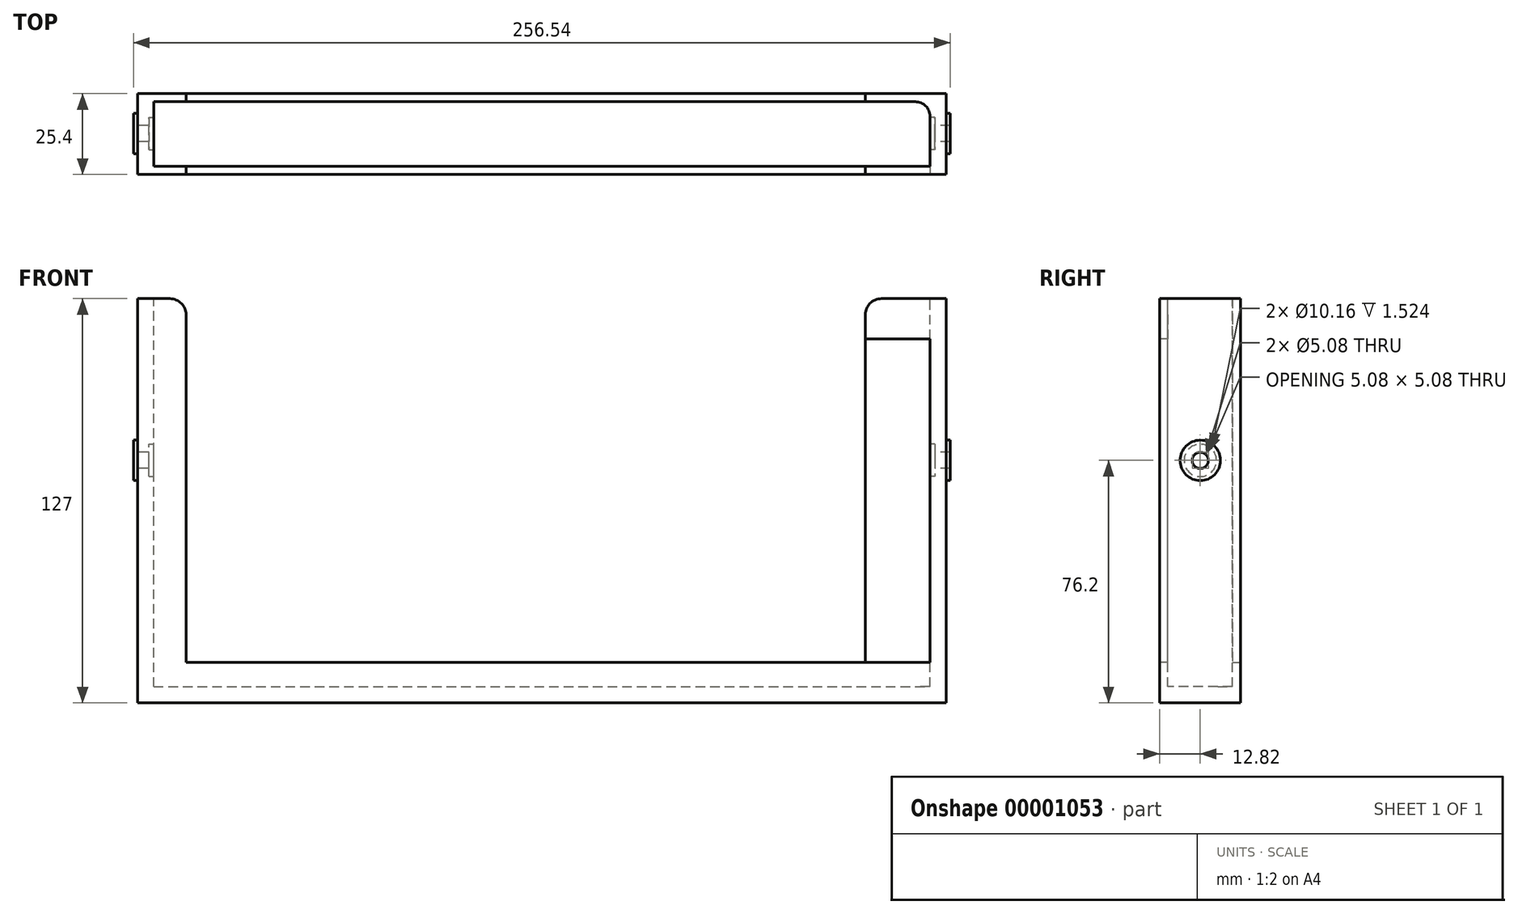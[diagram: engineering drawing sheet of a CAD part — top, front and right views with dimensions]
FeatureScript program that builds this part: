
annotation { "Feature Type Name" : "Feature", "Feature Type Description" : "" }
export const myFeature = defineFeature(function(context is Context, id is Id, definition is map)
    precondition{}
    {
        {
            var Q0;
            Q0=qCreatedBy(makeId("Front.planeOp"),FACE);
            var sketch = newSketch(context, id + "F0", { "sketchPlane" : qUnion([Q0])});
            skLineSegment(sketch, "E0", {"start": v(-127, 127) * mm, "end": v(-127, 0) * mm});
            skLineSegment(sketch, "E1", {"start": v(-127, 0) * mm, "end": v(127, 0) * mm});
            skLineSegment(sketch, "E2", {"start": v(127, 0) * mm, "end": v(127, 127) * mm});
            skLineSegment(sketch, "E3", {"start": v(127, 127) * mm, "end": v(101.6, 127) * mm});
            skLineSegment(sketch, "E4", {"start": v(101.6, 127) * mm, "end": v(101.6, 12.7) * mm});
            skLineSegment(sketch, "E5", {"start": v(101.6, 12.7) * mm, "end": v(-111.76, 12.7) * mm});
            skLineSegment(sketch, "E6", {"start": v(-111.76, 12.7) * mm, "end": v(-111.76, 127) * mm});
            skLineSegment(sketch, "E7", {"start": v(-111.76, 127) * mm, "end": v(-127, 127) * mm});
            skSolve(sketch);
        }
        {
            var Q0;
            Q0=makeQuery(id+"F0.imprint","IMPRINT",FACE,{"disambiguationData":[TD([[makeQuery(id+"F0.imprint","IMPRINT",EDGE,{"derivedFrom":sQuery(id+"F0.wireOp",EDGE,"E0")}),1.0]])]});
            extrude(context, id + "F1", {"entities" : qUnion([Q0]), "depth" : 25.4 * mm});
        }
        {
            var Q0;
            Q0=makeQuery(id+"F1.opExtrude","SWEPT_FACE",FACE,{"disambiguationData":[OSD([sQuery(id+"F0.wireOp",EDGE,"E7")])]});
            var sketch = newSketch(context, id + "F2", { "sketchPlane" : qUnion([Q0])});
            skLineSegment(sketch, "E8.bottom", {"start": v(-121.92, -2.54) * mm, "end": v(121.92, -2.54) * mm});
            skLineSegment(sketch, "E8.top", {"start": v(-121.92, -22.86) * mm, "end": v(121.92, -22.86) * mm});
            skLineSegment(sketch, "E8.left", {"start": v(-121.92, -2.54) * mm, "end": v(-121.92, -22.86) * mm});
            skLineSegment(sketch, "E8.right", {"start": v(121.92, -2.54) * mm, "end": v(121.92, -22.86) * mm});
            skSolve(sketch);
        }
        {
            var Q0;
            Q0 = qSketchRegion(id + "F2", true);
            var Q1;
            Q1=makeQuery(id+"F1.opExtrude","SWEPT_FACE",FACE,{"disambiguationData":[OSD([sQuery(id+"F0.wireOp",EDGE,"E5")])]});
            extrude(context, id + "F3", {"entities" : qUnion([Q0]), "operationType" : NewBodyOperationType.REMOVE, "oppositeDirection" : true, "endBoundEntity" : qUnion([Q1]), "depth" : 121.92 * mm});
        }
        {
            var Q0;
            Q0=makeQuery(id+"F3.boolean.opBoolean","COPY",EDGE,{"derivedFrom":makeQuery(id+"F3.opExtrude","SWEPT_EDGE",EDGE,{"disambiguationData":[OSD([sQuery(id+"F2.wireOp",EDGE,"E8.bottom"),sQuery(id+"F2.wireOp",EDGE,"E8.right")])]})});
            fillet(context, id + "F4", {"entities" : qUnion([Q0]), "radius" : 4.57 * mm, "tangentPropagation" : true, "allowEdgeOverflow" : false});
        }
        {
            var Q0;
            {var subQ0=sQuery(id+"F0.wireOp",EDGE,"E4");Q0=makeQuery(id+"F3.boolean.opBoolean","SPLIT",FACE,{"disambiguationData":[TD([makeQuery(id+"F3.opExtrude","SWEPT_FACE",FACE,{"disambiguationData":[OSD([sQuery(id+"F2.wireOp",EDGE,"E8.top")])]})])],"derivedFrom":makeQuery(id+"F1.opExtrude","SWEPT_FACE",FACE,{"disambiguationData":[OSD([subQ0])]})});}
            var sketch = newSketch(context, id + "F5", { "sketchPlane" : qUnion([Q0])});
            skLineSegment(sketch, "E9.bottom", {"start": v(22.86, 12.7) * mm, "end": v(25.4, 12.7) * mm});
            skLineSegment(sketch, "E9.top", {"start": v(22.86, 114.3) * mm, "end": v(25.4, 114.3) * mm});
            skLineSegment(sketch, "E9.left", {"start": v(22.86, 12.7) * mm, "end": v(22.86, 114.3) * mm});
            skLineSegment(sketch, "E9.right", {"start": v(25.4, 12.7) * mm, "end": v(25.4, 114.3) * mm});
            skSolve(sketch);
        }
        {
            var Q0;
            Q0 = qSketchRegion(id + "F5", true);
            var Q1;
            Q1=makeQuery(id+"F3.boolean.opBoolean","COPY",FACE,{"derivedFrom":makeQuery(id+"F3.opExtrude","SWEPT_FACE",FACE,{"disambiguationData":[OSD([sQuery(id+"F2.wireOp",EDGE,"E8.right")])]})});
            extrude(context, id + "F6", {"entities" : qUnion([Q0]), "operationType" : NewBodyOperationType.REMOVE, "endBound" : BoundingType.UP_TO_SURFACE, "oppositeDirection" : true, "endBoundEntityFace" : qUnion([Q1]), "depth" : 25.4 * mm});
        }
        {
            var Q0;
            {var subQ0=sQuery(id+"F0.wireOp",EDGE,"E6");var subQ1=sQuery(id+"F0.wireOp",EDGE,"E7");Q0=makeQuery(id+"F3.boolean.opBoolean","SPLIT",EDGE,{"disambiguationData":[TD([makeQuery(id+"F3.opExtrude","SWEPT_FACE",FACE,{"disambiguationData":[OSD([sQuery(id+"F2.wireOp",EDGE,"E8.top")])]})])],"derivedFrom":makeQuery(id+"F1.opExtrude","SWEPT_EDGE",EDGE,{"disambiguationData":[OSD([subQ0,subQ1])]})});}
            var Q1;
            {var subQ0=sQuery(id+"F0.wireOp",EDGE,"E6");var subQ1=sQuery(id+"F0.wireOp",EDGE,"E7");Q1=makeQuery(id+"F3.boolean.opBoolean","SPLIT",EDGE,{"disambiguationData":[TD([makeQuery(id+"F3.opExtrude","SWEPT_FACE",FACE,{"disambiguationData":[OSD([sQuery(id+"F2.wireOp",EDGE,"E8.bottom")])]})])],"derivedFrom":makeQuery(id+"F1.opExtrude","SWEPT_EDGE",EDGE,{"disambiguationData":[OSD([subQ0,subQ1])]})});}
            var Q2;
            {var subQ0=sQuery(id+"F0.wireOp",EDGE,"E3");var subQ1=sQuery(id+"F0.wireOp",EDGE,"E4");Q2=makeQuery(id+"F3.boolean.opBoolean","SPLIT",EDGE,{"disambiguationData":[TD([makeQuery(id+"F3.opExtrude","SWEPT_FACE",FACE,{"disambiguationData":[OSD([sQuery(id+"F2.wireOp",EDGE,"E8.top")])]})])],"derivedFrom":makeQuery(id+"F1.opExtrude","SWEPT_EDGE",EDGE,{"disambiguationData":[OSD([subQ0,subQ1])]})});}
            var Q3;
            {var subQ0=sQuery(id+"F0.wireOp",EDGE,"E3");var subQ1=sQuery(id+"F0.wireOp",EDGE,"E4");Q3=makeQuery(id+"F3.boolean.opBoolean","SPLIT",EDGE,{"disambiguationData":[TD([makeQuery(id+"F3.opExtrude","SWEPT_FACE",FACE,{"disambiguationData":[OSD([sQuery(id+"F2.wireOp",EDGE,"E8.bottom")])]})])],"derivedFrom":makeQuery(id+"F1.opExtrude","SWEPT_EDGE",EDGE,{"disambiguationData":[OSD([subQ0,subQ1])]})});}
            var Q4;
            Q4=makeQuery(id+"F6.boolean.opBoolean","COPY",EDGE,{"derivedFrom":makeQuery(id+"F6.opExtrude","CAP_EDGE",EDGE,{"disambiguationData":[OSD([sQuery(id+"F5.wireOp",EDGE,"E9.top")])],"isStart":true})});
            fillet(context, id + "F7", {"entities" : qUnion([Q0, Q1, Q2, Q3, Q4]), "radius" : 5.08 * mm, "tangentPropagation" : true, "allowEdgeOverflow" : false});
        }
        {
            var Q0;
            Q0=makeQuery(id+"F6.boolean.opBoolean","MERGE",FACE,{"derivedFrom":[makeQuery(id+"F3.boolean.opBoolean","COPY",FACE,{"derivedFrom":makeQuery(id+"F3.opExtrude","SWEPT_FACE",FACE,{"disambiguationData":[OSD([sQuery(id+"F2.wireOp",EDGE,"E8.right")])]})}),makeQuery(id+"F6.opExtrude","CAP_FACE",FACE,{"disambiguationData":[OSD([sQuery(id+"F5.wireOp",EDGE,"E9.bottom"),sQuery(id+"F5.wireOp",EDGE,"E9.top"),sQuery(id+"F5.wireOp",EDGE,"E9.left"),sQuery(id+"F5.wireOp",EDGE,"E9.right")])],"isStart":false})]});
            var sketch = newSketch(context, id + "F8", { "sketchPlane" : qUnion([Q0])});
            skCircle(sketch, "E10", {"center": v(12.58, 76.2) * mm, "radius": 5.08 * mm});
            skSolve(sketch);
        }
        {
            var Q0;
            Q0=makeQuery(id+"F8.imprint","IMPRINT",FACE,{"disambiguationData":[TD([[makeQuery(id+"F8.imprint","IMPRINT",EDGE,{"derivedFrom":sQuery(id+"F8.wireOp",EDGE,"E10")}),1.0]])]});
            extrude(context, id + "F9", {"entities" : qUnion([Q0]), "operationType" : NewBodyOperationType.REMOVE, "oppositeDirection" : true, "depth" : 1.52 * mm});
        }
        {
            var Q0;
            Q0=makeQuery(id+"F3.boolean.opBoolean","COPY",FACE,{"derivedFrom":makeQuery(id+"F3.opExtrude","SWEPT_FACE",FACE,{"disambiguationData":[OSD([sQuery(id+"F2.wireOp",EDGE,"E8.left")])]})});
            var sketch = newSketch(context, id + "F10", { "sketchPlane" : qUnion([Q0])});
            skCircle(sketch, "E11", {"center": v(-12.58, 76.2) * mm, "radius": 5.08 * mm});
            skSolve(sketch);
        }
        {
            var Q0;
            Q0 = qSketchRegion(id + "F10", true);
            extrude(context, id + "F11", {"entities" : qUnion([Q0]), "operationType" : NewBodyOperationType.REMOVE, "oppositeDirection" : true, "depth" : 1.52 * mm});
        }
        {
            var Q0;
            Q0=makeQuery(id+"F1.opExtrude","SWEPT_FACE",FACE,{"disambiguationData":[OSD([sQuery(id+"F0.wireOp",EDGE,"E0")])]});
            var sketch = newSketch(context, id + "F12", { "sketchPlane" : qUnion([Q0])});
            skCircle(sketch, "E12", {"center": v(12.58, 76.2) * mm, "radius": 6.35 * mm});
            skSolve(sketch);
        }
        {
            var Q0;
            Q0 = qSketchRegion(id + "F12", true);
            extrude(context, id + "F13", {"entities" : qUnion([Q0]), "operationType" : NewBodyOperationType.ADD, "depth" : 1.27 * mm});
        }
        {
            var Q0;
            Q0=makeQuery(id+"F1.opExtrude","SWEPT_FACE",FACE,{"disambiguationData":[OSD([sQuery(id+"F0.wireOp",EDGE,"E2")])]});
            var sketch = newSketch(context, id + "F14", { "sketchPlane" : qUnion([Q0])});
            skCircle(sketch, "E13", {"center": v(-12.58, 76.2) * mm, "radius": 6.35 * mm});
            skSolve(sketch);
        }
        {
            var Q0;
            Q0 = qSketchRegion(id + "F14", true);
            extrude(context, id + "F15", {"entities" : qUnion([Q0]), "operationType" : NewBodyOperationType.ADD, "depth" : 1.27 * mm});
        }
        {
            var Q0;
            Q0=makeQuery(id+"F13.opExtrude","CAP_FACE",FACE,{"disambiguationData":[OSD([sQuery(id+"F12.wireOp",EDGE,"E12")])],"isStart":false});
            var sketch = newSketch(context, id + "F16", { "sketchPlane" : qUnion([Q0])});
            skCircle(sketch, "E14", {"center": v(12.58, 76.2) * mm, "radius": 2.54 * mm});
            skSolve(sketch);
        }
        {
            var Q0;
            Q0 = qSketchRegion(id + "F16", true);
            extrude(context, id + "F17", {"entities" : qUnion([Q0]), "operationType" : NewBodyOperationType.REMOVE, "endBound" : BoundingType.THROUGH_ALL, "oppositeDirection" : true, "depth" : 25.4 * mm});
        }
    });
